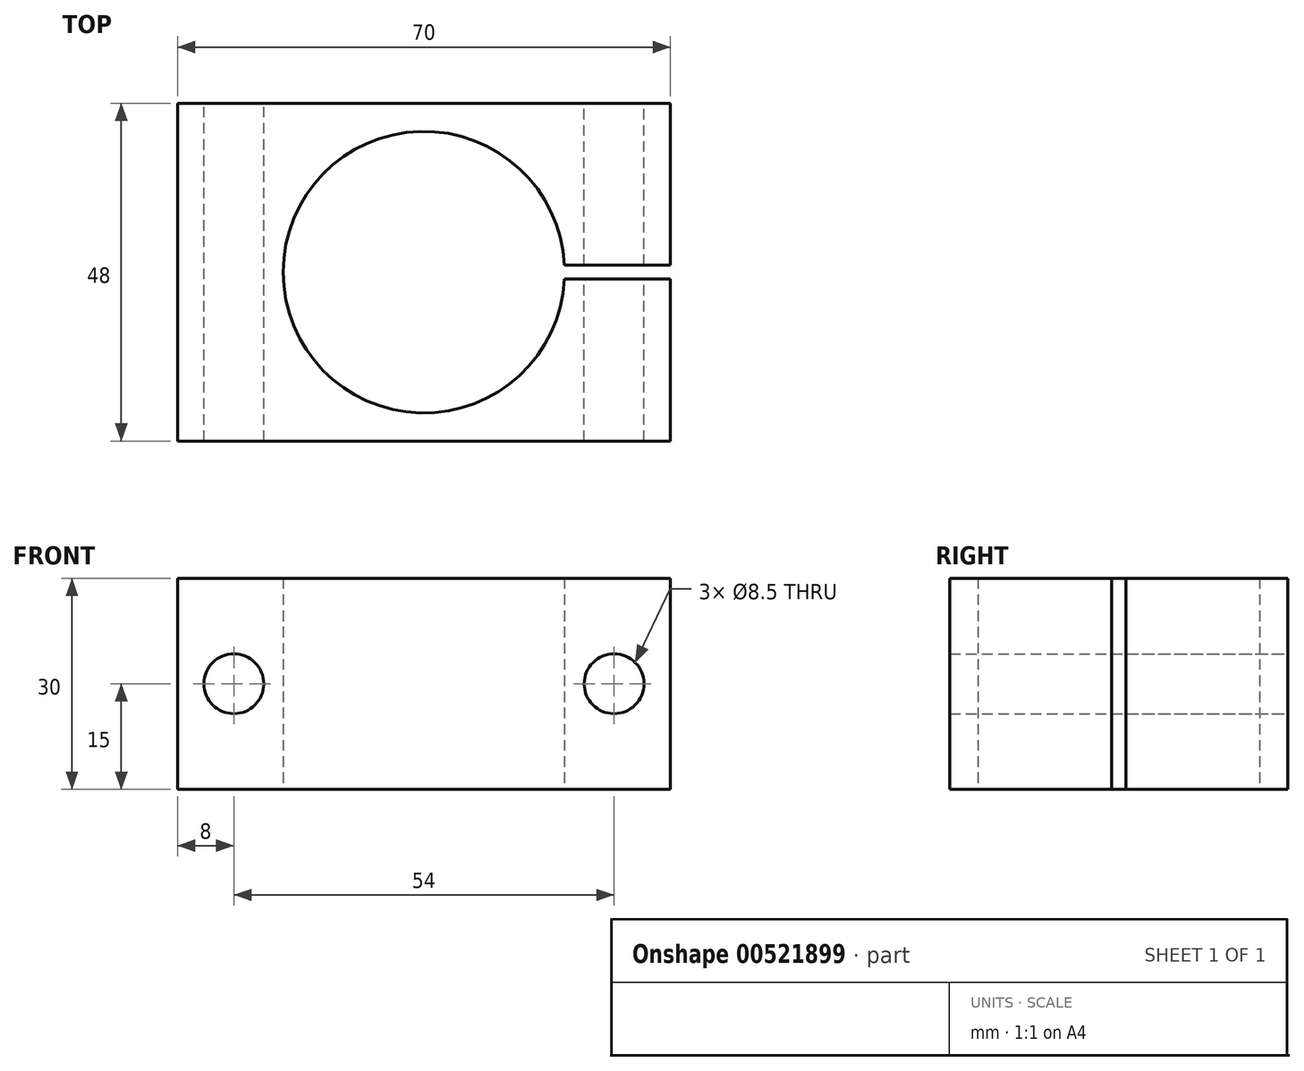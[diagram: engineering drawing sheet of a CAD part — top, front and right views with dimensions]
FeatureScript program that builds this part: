
annotation { "Feature Type Name" : "Feature", "Feature Type Description" : "" }
export const myFeature = defineFeature(function(context is Context, id is Id, definition is map)
    precondition{}
    {
        {
            var Q0;
            Q0=qCreatedBy(makeId("Top.planeOp"),FACE);
            var sketch = newSketch(context, id + "F0", { "sketchPlane" : qUnion([Q0])});
            skLineSegment(sketch, "E0.bottom", {"start": v(-35, 24) * mm, "end": v(35, 24) * mm});
            skLineSegment(sketch, "E0.top", {"start": v(-35, -24) * mm, "end": v(35, -24) * mm});
            skLineSegment(sketch, "E0.left", {"start": v(-35, 24) * mm, "end": v(-35, -24) * mm});
            skLineSegment(sketch, "E0.right", {"start": v(35, 24) * mm, "end": v(35, 1) * mm});
            skArc(sketch, "E1", {"start": v(19.97, 1) * mm, "mid": v(-20, 0) * mm, "end": v(19.97, -1) * mm});
            skLineSegment(sketch, "E2", {"start": v(35, 1) * mm, "end": v(19.97, 1) * mm});
            skLineSegment(sketch, "E3", {"start": v(19.97, -1) * mm, "end": v(35, -1) * mm});
            skLineSegment(sketch, "E4.trimOffspring", {"start": v(35, -1) * mm, "end": v(35, -24) * mm});
            skSolve(sketch);
        }
        {
            var Q0;
            Q0 = qSketchRegion(id + "F0", true);
            extrude(context, id + "F1", {"entities" : qUnion([Q0]), "depth" : 30 * mm, "offsetDistance" : 25 * mm});
        }
        {
            var Q0;
            Q0=makeQuery(id+"F1.opExtrude","SWEPT_FACE",FACE,{"disambiguationData":[OSD([sQuery(id+"F0.wireOp",EDGE,"E0.bottom")])]});
            var sketch = newSketch(context, id + "F2", { "sketchPlane" : qUnion([Q0])});
            skCircle(sketch, "E5", {"center": v(27, 15) * mm, "radius": 4.25 * mm});
            skPoint(sketch, "E5.centerSnap0", {"position": v(35, 15) * mm});
            skCircle(sketch, "E6", {"center": v(-27, 15) * mm, "radius": 4.25 * mm});
            skSolve(sketch);
        }
        {
            var Q0;
            Q0 = qSketchRegion(id + "F2", true);
            extrude(context, id + "F3", {"entities" : qUnion([Q0]), "operationType" : NewBodyOperationType.REMOVE, "endBound" : BoundingType.THROUGH_ALL, "oppositeDirection" : true, "depth" : 25 * mm, "offsetDistance" : 25 * mm});
        }
    });
